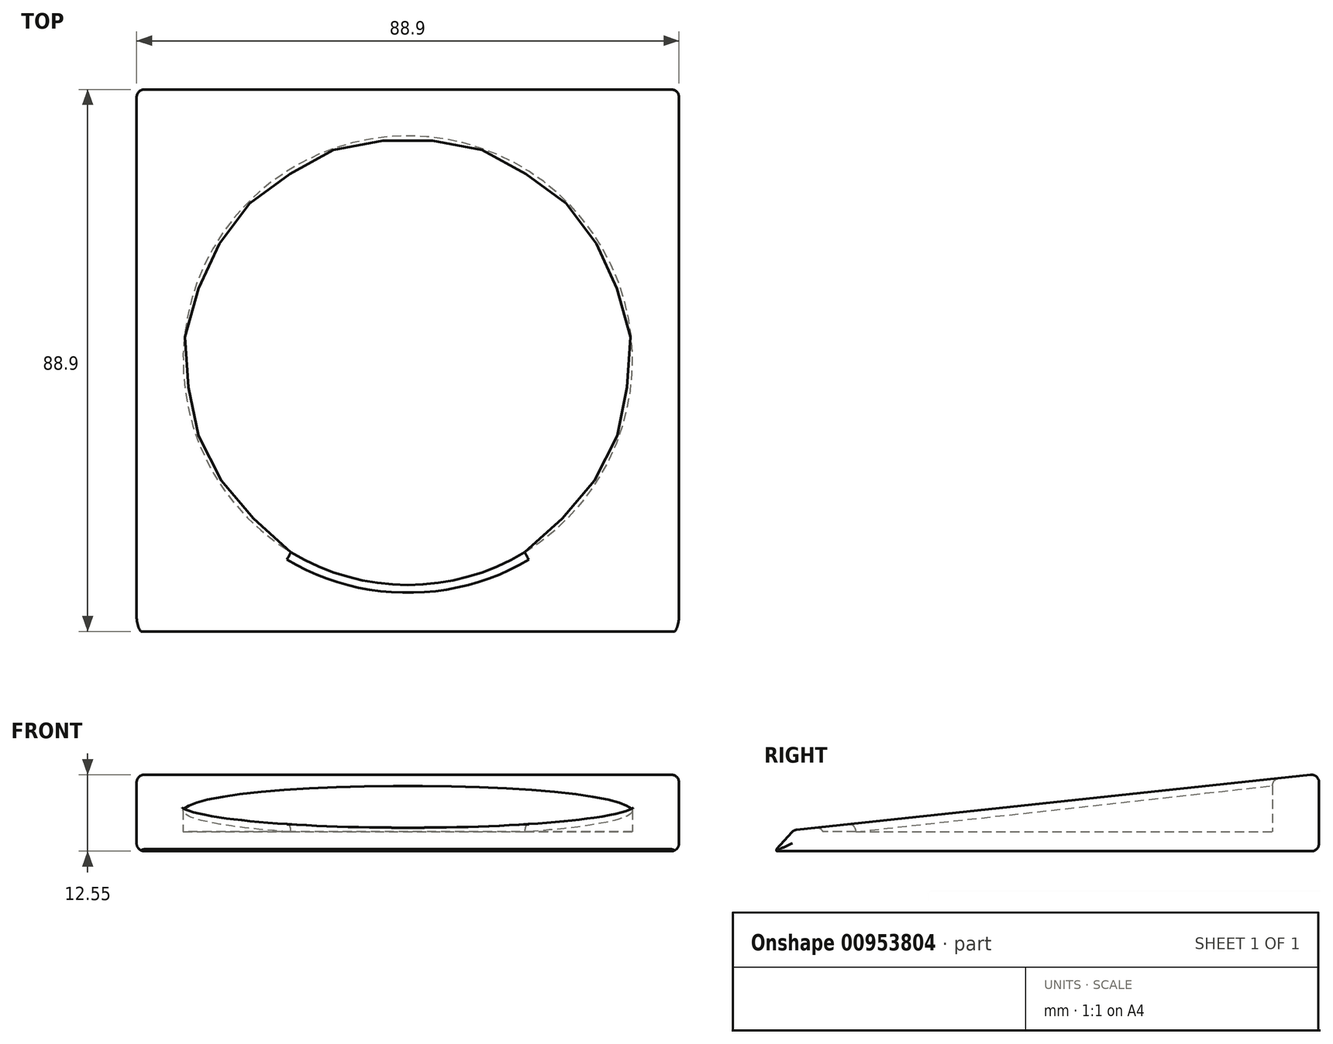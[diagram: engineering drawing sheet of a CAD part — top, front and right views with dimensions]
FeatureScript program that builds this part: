
annotation { "Feature Type Name" : "Feature", "Feature Type Description" : "" }
export const myFeature = defineFeature(function(context is Context, id is Id, definition is map)
    precondition{}
    {
        {
            var Q0;
            Q0=qCreatedBy(makeId("Right.planeOp"),FACE);
            var sketch = newSketch(context, id + "F0", { "sketchPlane" : qUnion([Q0])});
            skLineSegment(sketch, "E0", {"start": v(-44.45, 0) * mm, "end": v(44.45, 0) * mm});
            skLineSegment(sketch, "E1", {"start": v(-44.45, 0) * mm, "end": v(44.45, 9.53) * mm});
            skLineSegment(sketch, "E2", {"start": v(44.45, 0) * mm, "end": v(44.45, 9.53) * mm});
            skSolve(sketch);
        }
        {
            var Q0;
            Q0 = qSketchRegion(id + "F0", true);
            extrude(context, id + "F1", {"entities" : qUnion([Q0]), "depth" : 44.45 * mm, "offsetDistance" : 25.4 * mm, "hasSecondDirection" : true, "secondDirectionOppositeDirection" : true, "secondDirectionDepth" : 44.45 * mm});
        }
        {
            var Q0;
            Q0=qCreatedBy(makeId("Top.planeOp"),FACE);
            var sketch = newSketch(context, id + "F2", { "sketchPlane" : qUnion([Q0])});
            skCircle(sketch, "E3", {"center": v(0, 0) * mm, "radius": 36.83 * mm});
            skSolve(sketch);
        }
        {
            var Q0;
            Q0 = qSketchRegion(id + "F2", true);
            extrude(context, id + "F3", {"entities" : qUnion([Q0]), "operationType" : NewBodyOperationType.REMOVE, "depth" : 25.4 * mm, "offsetDistance" : 25.4 * mm});
        }
        {
            var Q0;
            Q0=makeQuery(id+"F1.opExtrude","SWEPT_FACE",FACE,{"disambiguationData":[OSD([sQuery(id+"F0.wireOp",EDGE,"E0")])]});
            var sketch = newSketch(context, id + "F4", { "sketchPlane" : qUnion([Q0])});
            skLineSegment(sketch, "E4.0.0", {"start": v(-44.45, 44.45) * mm, "end": v(-44.45, -44.45) * mm});
            skLineSegment(sketch, "E4.0.1", {"start": v(-44.45, -44.45) * mm, "end": v(44.45, -44.45) * mm});
            skLineSegment(sketch, "E4.0.2", {"start": v(44.45, -44.45) * mm, "end": v(44.45, 44.45) * mm});
            skLineSegment(sketch, "E4.0.3", {"start": v(44.45, 44.45) * mm, "end": v(-44.45, 44.45) * mm});
            skSolve(sketch);
        }
        {
            var Q0;
            Q0 = qSketchRegion(id + "F4", true);
            extrude(context, id + "F5", {"entities" : qUnion([Q0]), "operationType" : NewBodyOperationType.ADD, "depth" : 3.17 * mm, "offsetDistance" : 25.4 * mm});
        }
        {
            var Q0;
            Q0=makeQuery(id+"F5.boolean.opBoolean","MERGE",EDGE,{"derivedFrom":[makeQuery(id+"F1.opExtrude","SWEPT_EDGE",EDGE,{"disambiguationData":[OSD([sQuery(id+"F0.wireOp",EDGE,"E0"),sQuery(id+"F0.wireOp",EDGE,"E1")])]}),makeQuery(id+"F5.opExtrude","CAP_EDGE",EDGE,{"disambiguationData":[OSD([sQuery(id+"F4.wireOp",EDGE,"E4.0.3")])],"isStart":true})]});
            chamfer(context, id + "F6", {"entities" : qUnion([Q0]), "width" : 3.17 * mm, "tangentPropagation" : true});
        }
        {
            var Q0;
            Q0=makeQuery(id+"F1.opExtrude","CAP_EDGE",EDGE,{"disambiguationData":[OSD([sQuery(id+"F0.wireOp",EDGE,"E1")])],"isStart":true});
            var Q1;
            Q1=makeQuery(id+"F1.opExtrude","SWEPT_EDGE",EDGE,{"disambiguationData":[OSD([sQuery(id+"F0.wireOp",EDGE,"E1"),sQuery(id+"F0.wireOp",EDGE,"E2")])]});
            var Q2;
            Q2=makeQuery(id+"F1.opExtrude","CAP_EDGE",EDGE,{"disambiguationData":[OSD([sQuery(id+"F0.wireOp",EDGE,"E1")])],"isStart":false});
            var Q3;
            {var subQ0=sQuery(id+"F0.wireOp",EDGE,"E1");var subQ1=sQuery(id+"F0.wireOp",EDGE,"E0");Q3=makeQuery(id+"F6.opChamfer","BLEND_EDGE",EDGE,{"blendedFrom":[makeQuery(id+"F5.boolean.opBoolean","MERGE",EDGE,{"derivedFrom":[makeQuery(id+"F1.opExtrude","SWEPT_EDGE",EDGE,{"disambiguationData":[OSD([subQ1,subQ0])]}),makeQuery(id+"F5.opExtrude","CAP_EDGE",EDGE,{"disambiguationData":[OSD([sQuery(id+"F4.wireOp",EDGE,"E4.0.3")])],"isStart":true})]}),makeQuery(id+"F5.boolean.opBoolean","MERGE",FACE,{"derivedFrom":[makeQuery(id+"F1.opExtrude","CAP_FACE",FACE,{"disambiguationData":[OSD([subQ1,subQ0,sQuery(id+"F0.wireOp",EDGE,"E2")])],"isStart":true}),makeQuery(id+"F5.opExtrude","SWEPT_FACE",FACE,{"disambiguationData":[OSD([sQuery(id+"F4.wireOp",EDGE,"E4.0.0")])]})]})],"blendedInto":[makeQuery(id+"F5.boolean.opBoolean","MERGE",FACE,{"derivedFrom":[makeQuery(id+"F1.opExtrude","CAP_FACE",FACE,{"disambiguationData":[OSD([subQ1,subQ0,sQuery(id+"F0.wireOp",EDGE,"E2")])],"isStart":true}),makeQuery(id+"F5.opExtrude","SWEPT_FACE",FACE,{"disambiguationData":[OSD([sQuery(id+"F4.wireOp",EDGE,"E4.0.0")])]})]})]});}
            var Q4;
            {var subQ0=sQuery(id+"F0.wireOp",EDGE,"E1");Q4=makeQuery(id+"F6.opChamfer","BLEND_EDGE",EDGE,{"blendedFrom":[makeQuery(id+"F5.boolean.opBoolean","MERGE",EDGE,{"derivedFrom":[makeQuery(id+"F1.opExtrude","SWEPT_EDGE",EDGE,{"disambiguationData":[OSD([sQuery(id+"F0.wireOp",EDGE,"E0"),subQ0])]}),makeQuery(id+"F5.opExtrude","CAP_EDGE",EDGE,{"disambiguationData":[OSD([sQuery(id+"F4.wireOp",EDGE,"E4.0.3")])],"isStart":true})]}),makeQuery(id+"F1.opExtrude","SWEPT_FACE",FACE,{"disambiguationData":[OSD([subQ0])]})],"blendedInto":[makeQuery(id+"F1.opExtrude","SWEPT_FACE",FACE,{"disambiguationData":[OSD([subQ0])]})]});}
            var Q5;
            {var subQ0=sQuery(id+"F4.wireOp",EDGE,"E4.0.3");Q5=makeQuery(id+"F6.opChamfer","BLEND_EDGE",EDGE,{"blendedFrom":[makeQuery(id+"F5.boolean.opBoolean","MERGE",EDGE,{"derivedFrom":[makeQuery(id+"F1.opExtrude","SWEPT_EDGE",EDGE,{"disambiguationData":[OSD([sQuery(id+"F0.wireOp",EDGE,"E0"),sQuery(id+"F0.wireOp",EDGE,"E1")])]}),makeQuery(id+"F5.opExtrude","CAP_EDGE",EDGE,{"disambiguationData":[OSD([subQ0])],"isStart":true})]}),makeQuery(id+"F5.opExtrude","CAP_FACE",FACE,{"disambiguationData":[OSD([sQuery(id+"F4.wireOp",EDGE,"E4.0.0"),sQuery(id+"F4.wireOp",EDGE,"E4.0.1"),sQuery(id+"F4.wireOp",EDGE,"E4.0.2"),subQ0])],"isStart":false})],"blendedInto":[makeQuery(id+"F5.opExtrude","CAP_FACE",FACE,{"disambiguationData":[OSD([sQuery(id+"F4.wireOp",EDGE,"E4.0.0"),sQuery(id+"F4.wireOp",EDGE,"E4.0.1"),sQuery(id+"F4.wireOp",EDGE,"E4.0.2"),subQ0])],"isStart":false})]});}
            var Q6;
            {var subQ0=sQuery(id+"F0.wireOp",EDGE,"E1");var subQ1=sQuery(id+"F0.wireOp",EDGE,"E0");Q6=makeQuery(id+"F6.opChamfer","BLEND_EDGE",EDGE,{"blendedFrom":[makeQuery(id+"F5.boolean.opBoolean","MERGE",EDGE,{"derivedFrom":[makeQuery(id+"F1.opExtrude","SWEPT_EDGE",EDGE,{"disambiguationData":[OSD([subQ1,subQ0])]}),makeQuery(id+"F5.opExtrude","CAP_EDGE",EDGE,{"disambiguationData":[OSD([sQuery(id+"F4.wireOp",EDGE,"E4.0.3")])],"isStart":true})]}),makeQuery(id+"F5.boolean.opBoolean","MERGE",FACE,{"derivedFrom":[makeQuery(id+"F1.opExtrude","CAP_FACE",FACE,{"disambiguationData":[OSD([subQ1,subQ0,sQuery(id+"F0.wireOp",EDGE,"E2")])],"isStart":false}),makeQuery(id+"F5.opExtrude","SWEPT_FACE",FACE,{"disambiguationData":[OSD([sQuery(id+"F4.wireOp",EDGE,"E4.0.2")])]})]})],"blendedInto":[makeQuery(id+"F5.boolean.opBoolean","MERGE",FACE,{"derivedFrom":[makeQuery(id+"F1.opExtrude","CAP_FACE",FACE,{"disambiguationData":[OSD([subQ1,subQ0,sQuery(id+"F0.wireOp",EDGE,"E2")])],"isStart":false}),makeQuery(id+"F5.opExtrude","SWEPT_FACE",FACE,{"disambiguationData":[OSD([sQuery(id+"F4.wireOp",EDGE,"E4.0.2")])]})]})]});}
            var Q7;
            Q7=makeQuery(id+"F5.opExtrude","CAP_EDGE",EDGE,{"disambiguationData":[OSD([sQuery(id+"F4.wireOp",EDGE,"E4.0.2")])],"isStart":false});
            var Q8;
            Q8=makeQuery(id+"F5.opExtrude","CAP_EDGE",EDGE,{"disambiguationData":[OSD([sQuery(id+"F4.wireOp",EDGE,"E4.0.1")])],"isStart":false});
            var Q9;
            Q9=makeQuery(id+"F5.opExtrude","CAP_EDGE",EDGE,{"disambiguationData":[OSD([sQuery(id+"F4.wireOp",EDGE,"E4.0.0")])],"isStart":false});
            var Q10;
            Q10=makeQuery(id+"F5.boolean.opBoolean","MERGE",EDGE,{"derivedFrom":[makeQuery(id+"F1.opExtrude","CAP_EDGE",EDGE,{"disambiguationData":[OSD([sQuery(id+"F0.wireOp",EDGE,"E2")])],"isStart":true}),makeQuery(id+"F5.opExtrude","SWEPT_EDGE",EDGE,{"disambiguationData":[OSD([sQuery(id+"F4.wireOp",EDGE,"E4.0.0"),sQuery(id+"F4.wireOp",EDGE,"E4.0.1")])]})]});
            var Q11;
            Q11=makeQuery(id+"F5.boolean.opBoolean","MERGE",EDGE,{"derivedFrom":[makeQuery(id+"F1.opExtrude","CAP_EDGE",EDGE,{"disambiguationData":[OSD([sQuery(id+"F0.wireOp",EDGE,"E2")])],"isStart":false}),makeQuery(id+"F5.opExtrude","SWEPT_EDGE",EDGE,{"disambiguationData":[OSD([sQuery(id+"F4.wireOp",EDGE,"E4.0.1"),sQuery(id+"F4.wireOp",EDGE,"E4.0.2")])]})]});
            var Q12;
            Q12=makeQuery(id+"F3.boolean.opBoolean","INTERSECT",EDGE,{"derivedFrom":[makeQuery(id+"F1.opExtrude","SWEPT_FACE",FACE,{"disambiguationData":[OSD([sQuery(id+"F0.wireOp",EDGE,"E1")])]}),makeQuery(id+"F3.opExtrude","SWEPT_FACE",FACE,{"disambiguationData":[OSD([sQuery(id+"F2.wireOp",EDGE,"E3")])]})]});
            fillet(context, id + "F7", {"entities" : qUnion([Q0, Q1, Q2, Q3, Q4, Q5, Q6, Q7, Q8, Q9, Q10, Q11, Q12]), "radius" : 1.27 * mm, "tangentPropagation" : true, "allowEdgeOverflow" : false});
        }
    });
